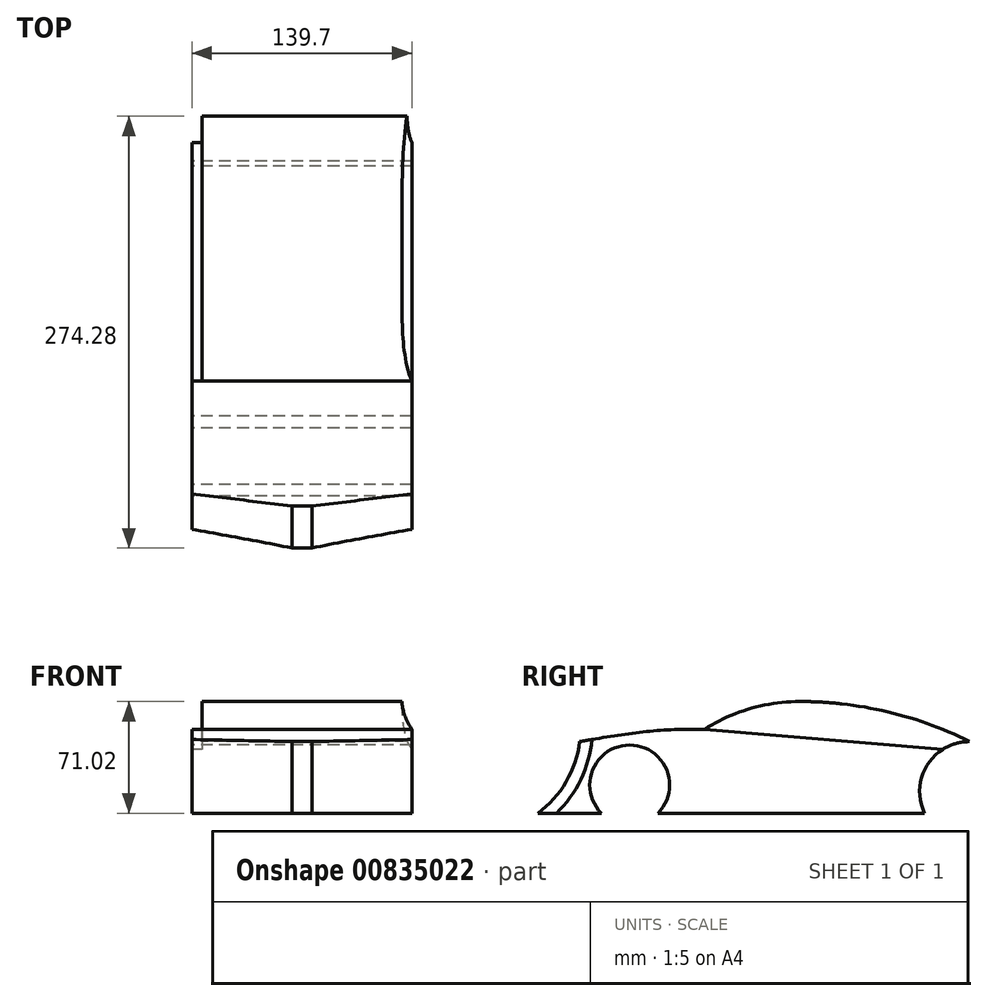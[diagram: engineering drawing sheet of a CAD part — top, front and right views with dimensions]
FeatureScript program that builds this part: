
annotation { "Feature Type Name" : "Feature", "Feature Type Description" : "" }
export const myFeature = defineFeature(function(context is Context, id is Id, definition is map)
    precondition{}
    {
        {
            var Q0;
            Q0=qCreatedBy(makeId("Right.planeOp"),FACE);
            var sketch = newSketch(context, id + "F0", { "sketchPlane" : qUnion([Q0])});
            skCircle(sketch, "E0", {"center": v(98.47, 0) * mm, "radius": 25.4 * mm});
            skLineSegment(sketch, "E1", {"start": v(-142.83, 0) * mm, "end": v(-149.18, 0) * mm, "construction": true});
            skLineSegment(sketch, "E2", {"start": v(-117.43, 25.4) * mm, "end": v(-117.43, 31.75) * mm, "construction": true});
            skArc(sketch, "E3", {"start": v(-117.43, 31.75) * mm, "mid": v(-144.33, 16.87) * mm, "end": v(-146.02, -13.81) * mm});
            skLineSegment(sketch, "E4", {"start": v(-149.18, 0) * mm, "end": v(-161.88, 0) * mm, "construction": true});
            skLineSegment(sketch, "E5", {"start": v(-117.43, 31.75) * mm, "end": v(-149.18, 31.75) * mm, "construction": true});
            skArc(sketch, "E6", {"start": v(-175.8, -13.81) * mm, "mid": v(-157.77, 6.2) * mm, "end": v(-149.18, 31.75) * mm});
            skLineSegment(sketch, "E7", {"start": v(-117.43, 31.75) * mm, "end": v(-117.43, 36.83) * mm, "construction": true});
            skLineSegment(sketch, "E8", {"start": v(-117.43, 31.75) * mm, "end": v(-60.28, 31.75) * mm, "construction": true});
            skLineSegment(sketch, "E9", {"start": v(-88.86, 31.75) * mm, "end": v(-88.86, 39.37) * mm, "construction": true});
            skFitSpline(sketch, "E10", {"points": [v(-149.18, 31.75) * mm, v(-117.43, 36.83) * mm, v(-88.86, 39.37) * mm, v(-60.28, 39.37) * mm], "startDerivative": vector(92.87, 16.03) * mm, "endDerivative": vector(87.84, -1.62) * mm});
            skLineSegment(sketch, "E11", {"start": v(-117.43, 0) * mm, "end": v(-117.43, -40.6) * mm, "construction": true});
            skArc(sketch, "E12", {"start": v(-9.48, 57.21) * mm, "mid": v(-40.93, 52.7) * mm, "end": v(-69.85, 39.53) * mm});
            skLineSegment(sketch, "E13", {"start": v(-9.48, 0) * mm, "end": v(-9.48, 32.93) * mm, "construction": true});
            skArc(sketch, "E14.MirrorCS", {"start": v(69.88, -13.81) * mm, "mid": v(71.58, 16.87) * mm, "end": v(98.47, 31.75) * mm});
            skArc(sketch, "E15", {"start": v(-9.48, 57.21) * mm, "mid": v(51.26, 49.45) * mm, "end": v(108.1, 26.66) * mm});
            skLineSegment(sketch, "E16", {"start": v(-117.43, 0) * mm, "end": v(-117.43, 4.15) * mm, "construction": true});
            skCircle(sketch, "E17", {"center": v(-117.43, 4.15) * mm, "radius": 25.4 * mm});
            skLineSegment(sketch, "E18", {"start": v(-117.43, 4.15) * mm, "end": v(-135.4, -13.81) * mm, "construction": true});
            skLineSegment(sketch, "E19", {"start": v(-175.8, -13.81) * mm, "end": v(-146.02, -13.81) * mm});
            skPoint(sketch, "E20.orphan", {"position": v(-149.18, -13.81) * mm});
            skPoint(sketch, "E21.orphan", {"position": v(130.22, 0) * mm});
            skArc(sketch, "E22.MirrorCS", {"start": v(-117.43, 31.75) * mm, "mid": v(-90.54, 16.87) * mm, "end": v(-88.84, -13.81) * mm});
            skLineSegment(sketch, "E23", {"start": v(-88.84, -13.81) * mm, "end": v(69.88, -13.81) * mm});
            skLineSegment(sketch, "E24", {"start": v(-69.85, 39.53) * mm, "end": v(81.6, 26.9) * mm});
            skLineSegment(sketch, "E25", {"start": v(45.98, 50.76) * mm, "end": v(-9.48, 34.5) * mm});
            skLineSegment(sketch, "E26", {"start": v(-146.02, -13.81) * mm, "end": v(-88.84, -13.81) * mm});
            skLineSegment(sketch, "E27", {"start": v(69.88, -13.81) * mm, "end": v(127.06, -13.81) * mm});
            skArc(sketch, "E28.trimOffspring", {"start": v(129.32, 7.5) * mm, "mid": v(130.04, -3.36) * mm, "end": v(127.06, -13.81) * mm});
            skPoint(sketch, "E29.orphan", {"position": v(98.47, 31.75) * mm});
            skPoint(sketch, "E30.visualSharp", {"position": v(115.33, 26.9) * mm});
            skArc(sketch, "E30.filletArc", {"start": v(129.32, 7.5) * mm, "mid": v(120.34, 21.46) * mm, "end": v(104.64, 26.9) * mm});
            skLineSegment(sketch, "E31", {"start": v(-117.43, 4.15) * mm, "end": v(-88.84, 13.81) * mm, "construction": true});
            skLineSegment(sketch, "E32", {"start": v(-88.84, 13.81) * mm, "end": v(69.88, 13.81) * mm});
            skLineSegment(sketch, "E33", {"start": v(-88.84, 13.81) * mm, "end": v(-88.86, 39.37) * mm});
            skSolve(sketch);
        }
        {
            var Q0;
            Q0=makeQuery(id+"F0.imprint","IMPRINT",FACE,{"disambiguationData":[TD([[makeQuery(id+"F0.imprint","IMPRINT",EDGE,{"derivedFrom":sQuery(id+"F0.wireOp",EDGE,"E3")}),-1.0]])]});
            extrude(context, id + "F1", {"entities" : qUnion([Q0]), "endBound" : BoundingType.SYMMETRIC, "depth" : 139.7 * mm, "offsetDistance" : 25.4 * mm});
        }
        {
            var Q0;
            {var subQ9=sQuery(id+"F0.wireOp",EDGE,"E28.trimOffspring");Q0=makeQuery(id+"F0.imprint","IMPRINT",FACE,{"disambiguationData":[TD([[makeQuery(id+"F0.imprint","IMPRINT",EDGE,{"derivedFrom":subQ9}),-1.0]])]});}
            var Q1;
            {var subQ0=sQuery(id+"F0.wireOp",EDGE,"E23");Q1=makeQuery(id+"F0.imprint","IMPRINT",FACE,{"disambiguationData":[TD([[makeQuery(id+"F0.imprint","IMPRINT",EDGE,{"derivedFrom":subQ0}),1.0]])]});}
            var Q2;
            {var subQ4=sQuery(id+"F0.wireOp",EDGE,"E3");Q2=makeQuery(id+"F0.imprint","IMPRINT",FACE,{"disambiguationData":[TD([[makeQuery(id+"F0.imprint","IMPRINT",EDGE,{"derivedFrom":subQ4}),1.0]])]});}
            extrude(context, id + "F2", {"entities" : qUnion([Q0, Q1, Q2]), "operationType" : NewBodyOperationType.ADD, "endBound" : BoundingType.SYMMETRIC, "depth" : 139.7 * mm, "offsetDistance" : 25.4 * mm});
        }
        {
            var Q0;
            {var subQ0=sQuery(id+"F0.wireOp",EDGE,"E25");Q0=makeQuery(id+"F0.imprint","IMPRINT",FACE,{"disambiguationData":[TD([[makeQuery(id+"F0.imprint","IMPRINT",EDGE,{"derivedFrom":subQ0}),1.0]])]});}
            var Q1;
            {var subQ0=sQuery(id+"F0.wireOp",EDGE,"E12");Q1=makeQuery(id+"F0.imprint","IMPRINT",FACE,{"disambiguationData":[TD([[makeQuery(id+"F0.imprint","IMPRINT",EDGE,{"derivedFrom":subQ0}),1.0]])]});}
            extrude(context, id + "F3", {"entities" : qUnion([Q0, Q1]), "operationType" : NewBodyOperationType.ADD, "endBound" : BoundingType.SYMMETRIC, "depth" : 127 * mm, "offsetDistance" : 25.4 * mm});
        }
        {
            var Q0;
            Q0=makeQuery(id+"F1.opExtrude","CAP_EDGE",EDGE,{"disambiguationData":[OSD([sQuery(id+"F0.wireOp",EDGE,"E6")])],"isStart":false});
            chamfer(context, id + "F4", {"entities" : qUnion([Q0]), "chamferType" : ChamferType.TWO_OFFSETS, "width1" : 63.5 * mm, "oppositeDirection" : false, "width2" : 7.62 * mm, "tangentPropagation" : true});
        }
        {
            var Q0;
            Q0=makeQuery(id+"F1.opExtrude","CAP_EDGE",EDGE,{"disambiguationData":[OSD([sQuery(id+"F0.wireOp",EDGE,"E6")])],"isStart":true});
            chamfer(context, id + "F5", {"entities" : qUnion([Q0]), "chamferType" : ChamferType.TWO_OFFSETS, "width1" : 7.62 * mm, "oppositeDirection" : false, "width2" : 63.5 * mm, "tangentPropagation" : true});
        }
        {
            var Q0;
            {var subQ6=sQuery(id+"F0.wireOp",EDGE,"E32");Q0=makeQuery(id+"F0.imprint","IMPRINT",FACE,{"disambiguationData":[TD([[makeQuery(id+"F0.imprint","IMPRINT",EDGE,{"derivedFrom":subQ6}),1.0]])]});}
            extrude(context, id + "F6", {"entities" : qUnion([Q0]), "operationType" : NewBodyOperationType.ADD, "endBound" : BoundingType.SYMMETRIC, "depth" : 139.7 * mm, "offsetDistance" : 25.4 * mm});
        }
        {
            var Q0;
            Q0=makeQuery(id+"F3.opExtrude","CAP_EDGE",EDGE,{"disambiguationData":[OSD([sQuery(id+"F0.wireOp",EDGE,"E24")])],"isStart":false});
            fillet(context, id + "F7", {"entities" : qUnion([Q0]), "radius" : 46.23 * mm, "tangentPropagation" : true, "allowEdgeOverflow" : false});
        }
    });
